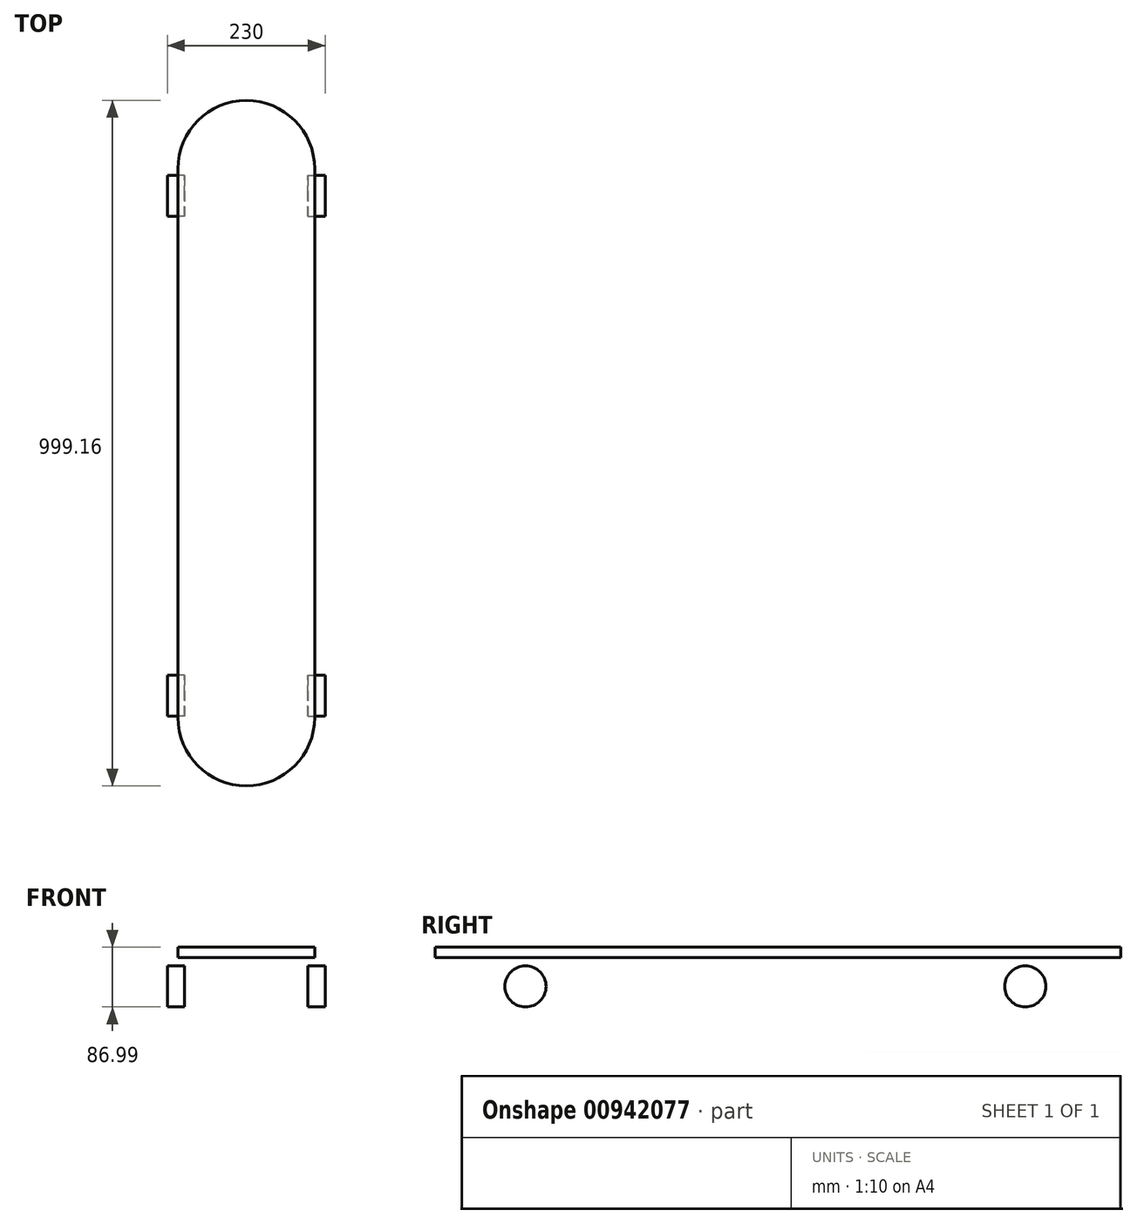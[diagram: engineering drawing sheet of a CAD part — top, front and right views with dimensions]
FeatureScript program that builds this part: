
annotation { "Feature Type Name" : "Feature", "Feature Type Description" : "" }
export const myFeature = defineFeature(function(context is Context, id is Id, definition is map)
    precondition{}
    {
        {
            var Q0;
            Q0=qCreatedBy(makeId("Top.planeOp"),FACE);
            var sketch = newSketch(context, id + "F0", { "sketchPlane" : qUnion([Q0])});
            skCircle(sketch, "E0", {"center": v(0, 0) * mm, "radius": 99.58 * mm});
            skLineSegment(sketch, "E1", {"start": v(0, 0) * mm, "end": v(0, -800) * mm, "construction": true});
            skCircle(sketch, "E2", {"center": v(0, -800) * mm, "radius": 99.58 * mm});
            skLineSegment(sketch, "E3", {"start": v(-99.58, -800) * mm, "end": v(-99.58, 0) * mm});
            skLineSegment(sketch, "E4", {"start": v(99.58, -800) * mm, "end": v(99.58, 0) * mm});
            skSolve(sketch);
        }
        {
            var Q0;
            Q0=qSketchRegion(id+"F0",true);
            extrude(context, id + "F1", {"entities" : qUnion([Q0]), "depth" : 15 * mm, "offsetDistance" : 25 * mm});
        }
        {
            var Q0;
            Q0=qCreatedBy(makeId("Right.planeOp"),FACE);
            cPlane(context, id + "F2", {"entities" : qUnion([Q0]), "cplaneType" : CPlaneType.OFFSET, "offset" : 115 * mm, "oppositeDirection" : true, "width" : 150 * mm, "height" : 150 * mm});
        }
        {
            var Q0;
            Q0=qCreatedBy(id+"F2.planeOp",FACE);
            var sketch = newSketch(context, id + "F3", { "sketchPlane" : qUnion([Q0])});
            skCircle(sketch, "E5", {"center": v(-39.69, -41.99) * mm, "radius": 30 * mm});
            skCircle(sketch, "E6", {"center": v(-767.85, -41.99) * mm, "radius": 30 * mm});
            skSolve(sketch);
        }
        {
            var Q0;
            Q0=qSketchRegion(id+"F3",true);
            extrude(context, id + "F4", {"entities" : qUnion([Q0]), "depth" : 25 * mm, "offsetDistance" : 25 * mm});
        }
        {
            var Q0;
            Q0=makeQuery(id+"F4.opExtrude","SWEPT_BODY",BODY,{"disambiguationData":[OSD([sQuery(id+"F3.wireOp",EDGE,"E5")])]});
            var Q1;
            Q1=makeQuery(id+"F4.opExtrude","SWEPT_BODY",BODY,{"disambiguationData":[OSD([sQuery(id+"F3.wireOp",EDGE,"E6")])]});
            var Q2;
            Q2=qCreatedBy(makeId("Right.planeOp"),FACE);
            mirror(context, id + "F5", {"entities" : qUnion([Q0, Q1]), "mirrorPlane" : qUnion([Q2])});
        }
    });
